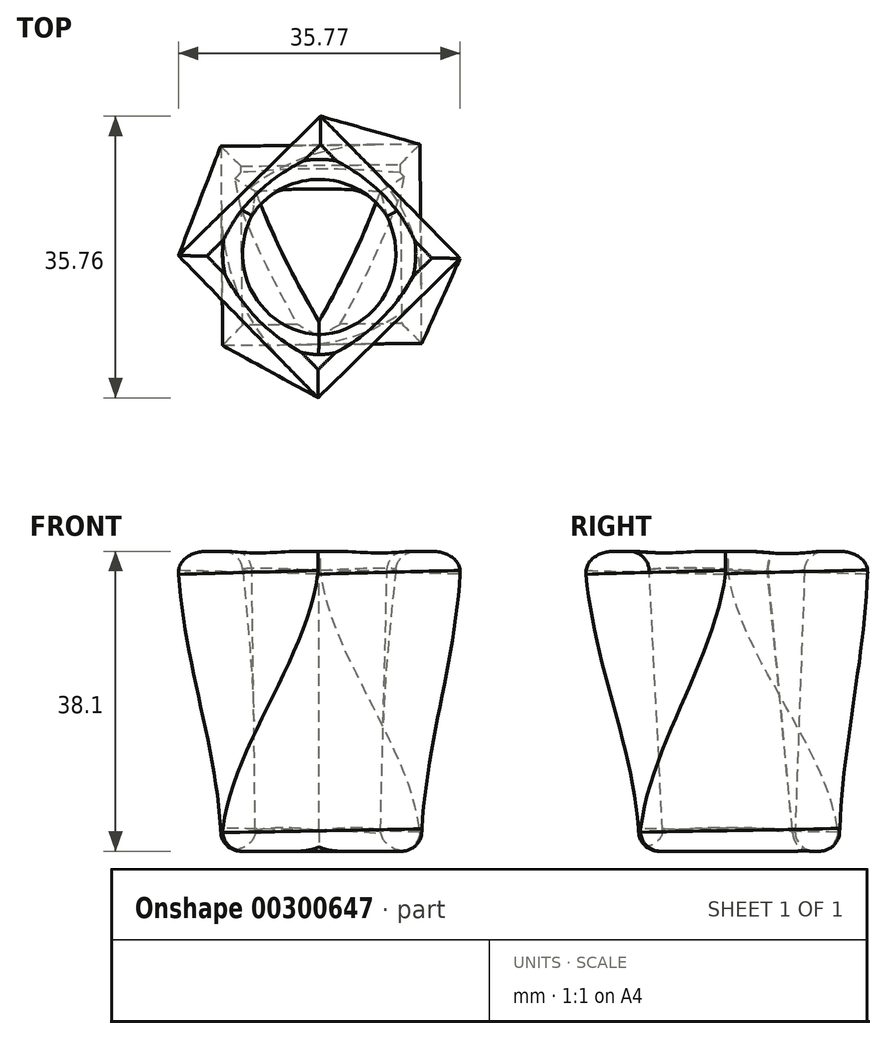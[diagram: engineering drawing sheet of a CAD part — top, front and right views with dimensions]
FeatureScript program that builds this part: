
annotation { "Feature Type Name" : "Feature", "Feature Type Description" : "" }
export const myFeature = defineFeature(function(context is Context, id is Id, definition is map)
    precondition{}
    {
        {
            var Q0;
            Q0=qCreatedBy(makeId("Top.planeOp"),FACE);
            var sketch = newSketch(context, id + "F0", { "sketchPlane" : qUnion([Q0])});
            skLineSegment(sketch, "E0.bottom", {"start": v(5.28, -10.11) * mm, "end": v(30.68, -10.11) * mm});
            skLineSegment(sketch, "E0.top", {"start": v(5.28, -35.51) * mm, "end": v(30.68, -35.51) * mm});
            skLineSegment(sketch, "E0.left", {"start": v(5.28, -10.11) * mm, "end": v(5.28, -35.51) * mm});
            skLineSegment(sketch, "E0.right", {"start": v(30.68, -10.11) * mm, "end": v(30.68, -35.51) * mm});
            skSolve(sketch);
        }
        {
            var Q0;
            Q0=qCreatedBy(makeId("Top.planeOp"),FACE);
            cPlane(context, id + "F1", {"entities" : qUnion([Q0]), "cplaneType" : CPlaneType.OFFSET, "offset" : 38.1 * mm, "width" : 152.4 * mm, "height" : 152.4 * mm});
        }
        {
            var Q0;
            Q0=qCreatedBy(id+"F1.planeOp",FACE);
            var sketch = newSketch(context, id + "F2", { "sketchPlane" : qUnion([Q0])});
            skLineSegment(sketch, "E1.0", {"start": v(-0.23, -24.41) * mm, "end": v(17.73, -6.45) * mm});
            skLineSegment(sketch, "E1.1", {"start": v(17.73, -6.45) * mm, "end": v(35.69, -24.41) * mm});
            skLineSegment(sketch, "E1.2", {"start": v(17.73, -42.37) * mm, "end": v(35.69, -24.41) * mm});
            skLineSegment(sketch, "E1.3", {"start": v(-0.23, -24.41) * mm, "end": v(17.73, -42.37) * mm});
            skSolve(sketch);
        }
        {
            var Q0;
            Q0 = qSketchRegion(id + "F0", true);
            var Q1;
            Q1 = qSketchRegion(id + "F2", true);
            loft(context, id + "F3", {"startCondition" : LoftEndDerivativeType.NORMAL_TO_PROFILE, "startMagnitude" : 1, "endCondition" : LoftEndDerivativeType.NORMAL_TO_PROFILE, "endMagnitude" : 1, "sheetProfilesArray" : [{ "sheetProfileEntities" : qUnion([Q0]) }, { "sheetProfileEntities" : qUnion([Q1]) }]});
        }
        {
            var Q0;
            Q0=makeQuery(id+"F3.opLoft","CAP_FACE",FACE,{"disambiguationData":[OSD([makeQuery(id+"F2.imprint","IMPRINT",FACE,{"disambiguationData":[TD([[makeQuery(id+"F2.imprint","IMPRINT",EDGE,{"derivedFrom":sQuery(id+"F2.wireOp",EDGE,"E1.0")}),-1.0]])]})])],"isStart":true});
            var sketch = newSketch(context, id + "F4", { "sketchPlane" : qUnion([Q0])});
            skLineSegment(sketch, "E2.0", {"start": v(35.69, -24.41) * mm, "end": v(17.73, -6.45) * mm});
            skLineSegment(sketch, "E2.1", {"start": v(17.73, -42.37) * mm, "end": v(35.69, -24.41) * mm});
            skLineSegment(sketch, "E2.2", {"start": v(-0.23, -24.41) * mm, "end": v(17.73, -42.37) * mm});
            skLineSegment(sketch, "E2.3", {"start": v(17.73, -6.45) * mm, "end": v(-0.23, -24.41) * mm});
            skCircle(sketch, "E3", {"center": v(17.73, -24.41) * mm, "radius": 9.97 * mm});
            skSolve(sketch);
        }
        {
            var Q0;
            Q0=makeQuery(id+"F0.imprint","IMPRINT",FACE,{"disambiguationData":[TD([[makeQuery(id+"F0.imprint","IMPRINT",EDGE,{"derivedFrom":sQuery(id+"F0.wireOp",EDGE,"E0.bottom")}),-1.0]])]});
            var sketch = newSketch(context, id + "F5", { "sketchPlane" : qUnion([Q0])});
            skLineSegment(sketch, "E4", {"start": v(17.68, -32.43) * mm, "end": v(9.63, -15.82) * mm});
            skLineSegment(sketch, "E5", {"start": v(9.63, -15.82) * mm, "end": v(25.43, -15.82) * mm});
            skLineSegment(sketch, "E6", {"start": v(25.43, -15.82) * mm, "end": v(17.68, -32.43) * mm});
            skSolve(sketch);
        }
        {
            var Q1;
            Q1=makeQuery(id+"F5.imprint","IMPRINT",FACE,{"disambiguationData":[TD([[makeQuery(id+"F5.imprint","IMPRINT",EDGE,{"derivedFrom":sQuery(id+"F5.wireOp",EDGE,"E4")}),-1.0]])]});
            var Q2;
            Q2=makeQuery(id+"F4.imprint","IMPRINT",FACE,{"disambiguationData":[TD([[makeQuery(id+"F4.imprint","IMPRINT",EDGE,{"derivedFrom":sQuery(id+"F4.wireOp",EDGE,"E3")}),1.0]])]});
            loft(context, id + "F6", {"operationType" : NewBodyOperationType.REMOVE, "sheetProfilesArray" : [{ "sheetProfileEntities" : qUnion([Q1]) }, { "sheetProfileEntities" : qUnion([Q2]) }]});
        }
        {
            var Q0;
            Q0=makeQuery(id+"F3.opLoft","CAP_FACE",FACE,{"disambiguationData":[OSD([makeQuery(id+"F2.imprint","IMPRINT",FACE,{"disambiguationData":[TD([[makeQuery(id+"F2.imprint","IMPRINT",EDGE,{"derivedFrom":sQuery(id+"F2.wireOp",EDGE,"E1.0")}),-1.0]])]})])],"isStart":true});
            var Q1;
            Q1=makeQuery(id+"F3.opLoft","CAP_FACE",FACE,{"disambiguationData":[OSD([makeQuery(id+"F0.imprint","IMPRINT",FACE,{"disambiguationData":[TD([[makeQuery(id+"F0.imprint","IMPRINT",EDGE,{"derivedFrom":sQuery(id+"F0.wireOp",EDGE,"E0.bottom")}),-1.0]])]})])],"isStart":true});
            fillet(context, id + "F7", {"entities" : qUnion([Q0, Q1]), "radius" : 2.54 * mm, "tangentPropagation" : true, "allowEdgeOverflow" : false});
        }
    });
